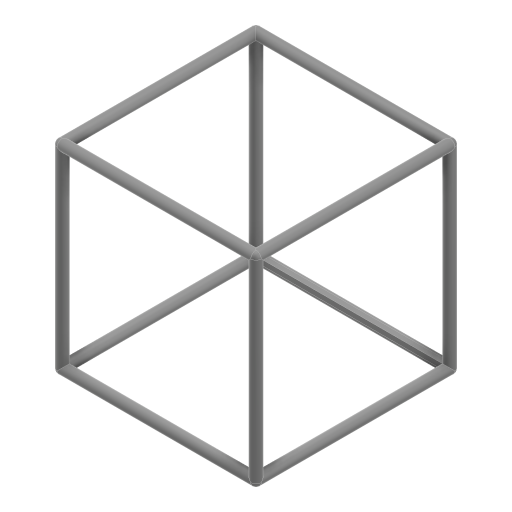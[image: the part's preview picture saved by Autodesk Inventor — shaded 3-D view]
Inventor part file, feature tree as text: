
AUTODESK INVENTOR PART (.ipt)
format: ipt  version: 2023 (Build 270158000, 158)  size: 210,944 bytes
history: native  units: in
note: dims shown in document units (in); Inventor stores cm internally (conversion verified against a paired STEP export)
features: extrude x4, sketch x4, projected_geometry x3, fillet x1
ambient origin geometry x8: Origin, YZ Plane, XZ Plane, XY Plane, X Axis, Y Axis, Z Axis, Center Point
bodies: Solid1 (feature_tree)
feature tree (12):
  extrude  "Extrusion1"  Depth=39.3701in TaperAngle=0.0deg
  extrude  "Extrusion2"  TaperAngle=0.0deg  [1 undecoded]
  extrude  "Extrusion3"  TaperAngle=0.0deg  [1 undecoded]
  extrude  "Extrusion4"  TaperAngle=0.0deg  [1 undecoded]
  fillet  "Fillet1"  Radius=1.0in
  sketch  "Sketch1"  dims[d0=39.3701in d2=39.3701in d3=0.0in]
  sketch  "Sketch2"  dims[d4=2.0in d5=0.0in d6=0.0in]
  projected_geometry  "Projected Loop1"
  sketch  "Sketch3"  dims[d7=2.0in d8=0.0in d9=0.0in]
  projected_geometry  "Projected Loop2"
  sketch  "Sketch4"  dims[d10=2.0in d11=0.0in d12=0.0in d13=1.0in]
  projected_geometry  "Projected Loop3"
note: 3 required parameter values undecoded (feature->parameter linkage not recoverable at this tier; creation-order binding heuristic only, values carry confidence <= 0.55)
